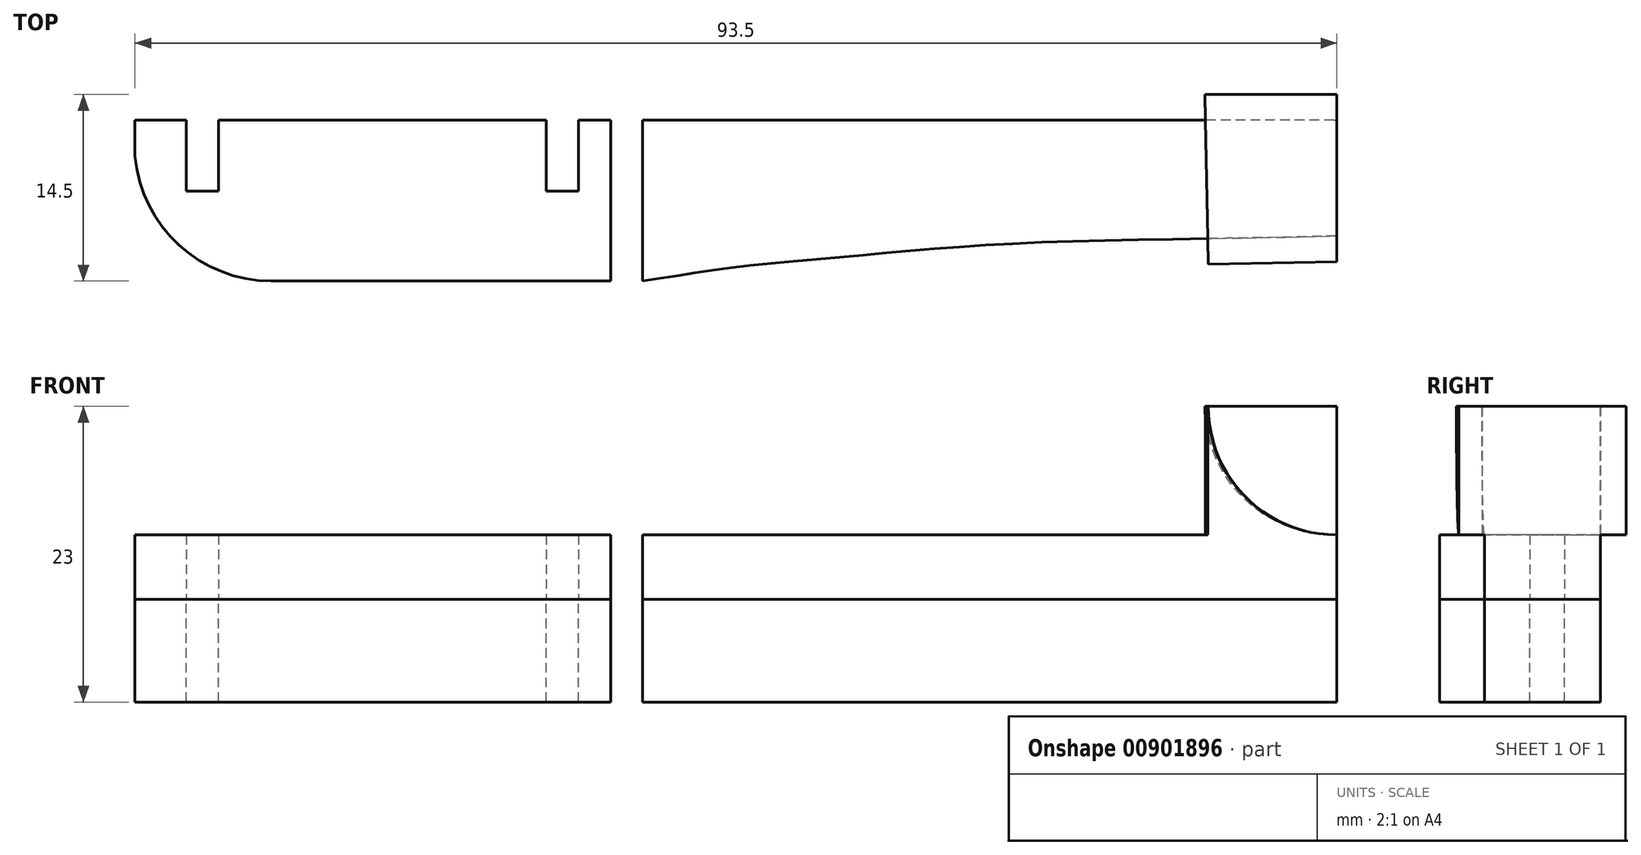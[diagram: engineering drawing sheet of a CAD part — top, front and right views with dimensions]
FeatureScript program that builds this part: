
annotation { "Feature Type Name" : "Feature", "Feature Type Description" : "" }
export const myFeature = defineFeature(function(context is Context, id is Id, definition is map)
    precondition{}
    {
        {
            var Q0;
            Q0=qCreatedBy(makeId("Top.planeOp"),FACE);
            var sketch = newSketch(context, id + "F0", { "sketchPlane" : qUnion([Q0])});
            skLineSegment(sketch, "E0", {"start": v(-34.28, 8.6) * mm, "end": v(-30.28, 8.6) * mm});
            skLineSegment(sketch, "E1", {"start": v(-30.28, 8.6) * mm, "end": v(-30.28, 3.1) * mm});
            skLineSegment(sketch, "E2", {"start": v(-30.28, 3.1) * mm, "end": v(-27.78, 3.1) * mm});
            skLineSegment(sketch, "E3", {"start": v(-27.78, 3.1) * mm, "end": v(-27.78, 8.6) * mm});
            skLineSegment(sketch, "E4", {"start": v(-27.78, 8.6) * mm, "end": v(-2.28, 8.6) * mm});
            skLineSegment(sketch, "E5", {"start": v(-2.28, 8.6) * mm, "end": v(-2.28, 3.1) * mm});
            skLineSegment(sketch, "E6", {"start": v(-2.28, 3.1) * mm, "end": v(0.22, 3.1) * mm});
            skLineSegment(sketch, "E7", {"start": v(0.22, 3.1) * mm, "end": v(0.22, 8.6) * mm});
            skLineSegment(sketch, "E8", {"start": v(0.22, 8.6) * mm, "end": v(2.72, 8.6) * mm});
            skLineSegment(sketch, "E9", {"start": v(2.72, 8.6) * mm, "end": v(2.72, -3.9) * mm});
            skLineSegment(sketch, "E10", {"start": v(2.72, -3.9) * mm, "end": v(-23.68, -3.9) * mm});
            skLineSegment(sketch, "E11", {"start": v(-34.28, 8.6) * mm, "end": v(-34.28, 5.81) * mm});
            skLineSegment(sketch, "E12", {"start": v(5.22, 8.6) * mm, "end": v(5.22, -3.9) * mm});
            skLineSegment(sketch, "E13", {"start": v(5.22, 8.6) * mm, "end": v(59.22, 8.6) * mm});
            skLineSegment(sketch, "E14", {"start": v(59.22, 10.6) * mm, "end": v(59.22, -2.4) * mm});
            skFitSpline(sketch, "E15", {"points": [v(5.22, -3.9) * mm, v(11.65, -2.92) * mm, v(21.83, -1.93) * mm, v(35.18, -0.94) * mm, v(59.22, -0.4) * mm], "startDerivative": vector(40.22, 5.62) * mm, "endDerivative": vector(72.07, 1.99) * mm});
            skArc(sketch, "E16", {"start": v(-34.28, 5.81) * mm, "mid": v(-30.86, -1.1) * mm, "end": v(-23.68, -3.9) * mm});
            skFitSpline(sketch, "E17.0", {"points": [v(5.5, -5.88) * mm, v(6.35, -5.76) * mm, v(7.52, -5.58) * mm, v(8.96, -5.34) * mm, v(10.02, -5.17) * mm, v(10.92, -5.03) * mm, v(11.58, -4.94) * mm, v(11.96, -4.9) * mm, v(12.36, -4.84) * mm, v(12.87, -4.78) * mm, v(13.71, -4.68) * mm, v(14.83, -4.57) * mm, v(16.23, -4.43) * mm, v(17.69, -4.3) * mm, v(19.18, -4.17) * mm, v(20.45, -4.06) * mm, v(21.47, -3.97) * mm, v(22.48, -3.88) * mm, v(23.75, -3.77) * mm, v(25.27, -3.63) * mm, v(26.8, -3.5) * mm, v(28.36, -3.37) * mm, v(29.97, -3.25) * mm, v(31.63, -3.13) * mm, v(33.08, -3.05) * mm, v(34.28, -2.98) * mm, v(35.2, -2.94) * mm, v(36.14, -2.9) * mm, v(37.44, -2.85) * mm, v(39.11, -2.8) * mm, v(41.2, -2.74) * mm, v(43.36, -2.7) * mm, v(46.3, -2.65) * mm, v(50.1, -2.59) * mm, v(54.7, -2.5) * mm, v(57.77, -2.44) * mm, v(59.27, -2.4) * mm]});
            skLineSegment(sketch, "E18.0", {"start": v(5.22, 10.6) * mm, "end": v(59.22, 10.6) * mm});
            skLineSegment(sketch, "E19.0", {"start": v(-36.28, 10.6) * mm, "end": v(-2.28, 10.6) * mm});
            skArc(sketch, "E20.0", {"start": v(-36.27, 5.63) * mm, "mid": v(-32.21, -2.57) * mm, "end": v(-23.68, -5.9) * mm});
            skLineSegment(sketch, "E21.0", {"start": v(-36.28, 10.6) * mm, "end": v(-36.28, 5.81) * mm});
            skLineSegment(sketch, "E22.0", {"start": v(5.4, -5.9) * mm, "end": v(-23.68, -5.9) * mm});
            skLineSegment(sketch, "E23", {"start": v(-2.28, 10.6) * mm, "end": v(5.22, 10.6) * mm});
            skLineSegment(sketch, "E24", {"start": v(5.5, -5.88) * mm, "end": v(5.4, -5.9) * mm});
            skLineSegment(sketch, "E25", {"start": v(-36.28, 5.81) * mm, "end": v(-36.27, 5.63) * mm});
            skLineSegment(sketch, "E26", {"start": v(-23.68, -5.9) * mm, "end": v(-23.68, -5.9) * mm});
            skSolve(sketch);
        }
        {
            var Q0;
            Q0=makeQuery(id+"F0.imprint","IMPRINT",FACE,{"disambiguationData":[TD([[makeQuery(id+"F0.imprint","IMPRINT",EDGE,{"derivedFrom":sQuery(id+"F0.wireOp",EDGE,"E0")}),-1.0]])]});
            var Q1;
            Q1=makeQuery(id+"F0.imprint","IMPRINT",FACE,{"disambiguationData":[TD([[makeQuery(id+"F0.imprint","IMPRINT",EDGE,{"derivedFrom":sQuery(id+"F0.wireOp",EDGE,"E12")}),1.0]])]});
            extrude(context, id + "F1", {"entities" : qUnion([Q0, Q1]), "oppositeDirection" : true, "depth" : 8 * mm, "offsetDistance" : 25 * mm});
        }
        {
            var Q0;
            Q0=makeQuery(id+"F0.imprint","IMPRINT",FACE,{"disambiguationData":[TD([[makeQuery(id+"F0.imprint","IMPRINT",EDGE,{"derivedFrom":sQuery(id+"F0.wireOp",EDGE,"E0")}),-1.0]])]});
            var Q1;
            Q1=makeQuery(id+"F0.imprint","IMPRINT",FACE,{"disambiguationData":[TD([[makeQuery(id+"F0.imprint","IMPRINT",EDGE,{"derivedFrom":sQuery(id+"F0.wireOp",EDGE,"E12")}),1.0]])]});
            var Q2;
            Q2=makeQuery(id+"F0.imprint","IMPRINT",FACE,{"disambiguationData":[TD([[makeQuery(id+"F0.imprint","IMPRINT",EDGE,{"derivedFrom":sQuery(id+"F0.wireOp",EDGE,"E0")}),1.0]])]});
            extrude(context, id + "F2", {"entities" : qUnion([Q0, Q1, Q2]), "depth" : 5 * mm, "offsetDistance" : 25 * mm});
        }
        {
            var Q0;
            Q0=makeQuery(id+"F2.opExtrude","CAP_FACE",FACE,{"disambiguationData":[OSD([sQuery(id+"F0.wireOp",EDGE,"E14"),sQuery(id+"F0.wireOp",EDGE,"E17.0"),sQuery(id+"F0.wireOp",EDGE,"E18.0"),sQuery(id+"F0.wireOp",EDGE,"E19.0"),sQuery(id+"F0.wireOp",EDGE,"E20.0"),sQuery(id+"F0.wireOp",EDGE,"E21.0"),sQuery(id+"F0.wireOp",EDGE,"E22.0"),sQuery(id+"F0.wireOp",EDGE,"E23"),sQuery(id+"F0.wireOp",EDGE,"E24"),sQuery(id+"F0.wireOp",EDGE,"E25"),sQuery(id+"F0.wireOp",EDGE,"E26")])],"isStart":false});
            var sketch = newSketch(context, id + "F3", { "sketchPlane" : qUnion([Q0])});
            skLineSegment(sketch, "E27", {"start": v(59.22, 10.6) * mm, "end": v(59.22, -2.4) * mm});
            skLineSegment(sketch, "E28", {"start": v(59.22, -2.4) * mm, "end": v(49.22, -2.6) * mm});
            skLineSegment(sketch, "E29", {"start": v(49.22, -2.6) * mm, "end": v(48.96, 10.6) * mm});
            skLineSegment(sketch, "E30", {"start": v(48.96, 10.6) * mm, "end": v(59.22, 10.6) * mm});
            skSolve(sketch);
        }
        {
            var Q0;
            Q0=makeQuery(id+"F3.imprint","IMPRINT",FACE,{"disambiguationData":[TD([[makeQuery(id+"F3.imprint","IMPRINT",EDGE,{"derivedFrom":sQuery(id+"F3.wireOp",EDGE,"E27")}),-1.0]])]});
            extrude(context, id + "F4", {"entities" : qUnion([Q0]), "operationType" : NewBodyOperationType.ADD, "depth" : 10 * mm, "offsetDistance" : 25 * mm});
        }
        {
            var Q0;
            Q0=makeQuery(id+"F4.opExtrude","CAP_EDGE",EDGE,{"disambiguationData":[OSD([sQuery(id+"F3.wireOp",EDGE,"E29")])],"isStart":true});
            fillet(context, id + "F5", {"entities" : qUnion([Q0]), "tangentPropagation" : true, "radius" : 10 * mm, "defaultsChanged" : true, "vertexSettings" : [], "allowEdgeOverflow" : false});
        }
    });
